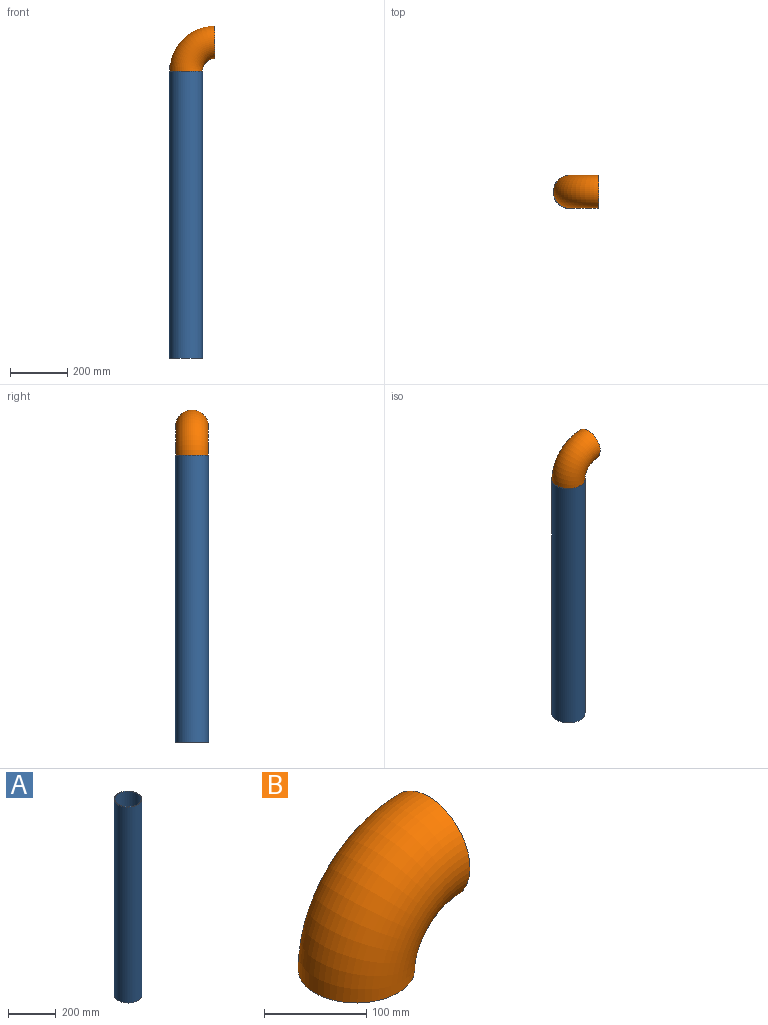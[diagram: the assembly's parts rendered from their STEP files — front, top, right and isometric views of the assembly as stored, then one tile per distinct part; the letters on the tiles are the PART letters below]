
ASSEMBLY  parts=2 mates=1
PART A: 4 faces, bbox 116x116x1000 mm
  f0: cylinder r=55mm len=1000mm, axis (0,0,-1), area 345575.2mm2, adj f2,f3
  f1: cylinder r=58mm len=1000mm, axis (0,0,-1), area 364424.7mm2, adj f2,f3
  f2: plane 116x116mm, normal (0,0,1), area 1065mm2, adj f0,f1
  f3: plane 116x116mm, normal (0,0,-1), area 1065mm2, adj f0,f1
PART B: 4 faces, bbox 169.9x114x169.9 mm
  f0: torus R=100mm, axis (0,1,0), area 54282.8mm2, adj f1,f2
  f1: plane 114x114mm, normal (0,0,-1), area 703.7mm2, adj f0,f3
  f2: plane 114x114mm, normal (1,0,0), area 703.7mm2, adj f0,f3
  f3: torus R=100mm, axis (0,1,0), area 56256.7mm2, adj f1,f2
PLACE A t=(-0.4,0.72,-498.45)mm
PLACE B t=(-0.4,0.8,501.55)mm
MATE fastened B.f1 <-> A.f0  axis (0,0,-1) through (-0.4,0.8,501.55)mm
